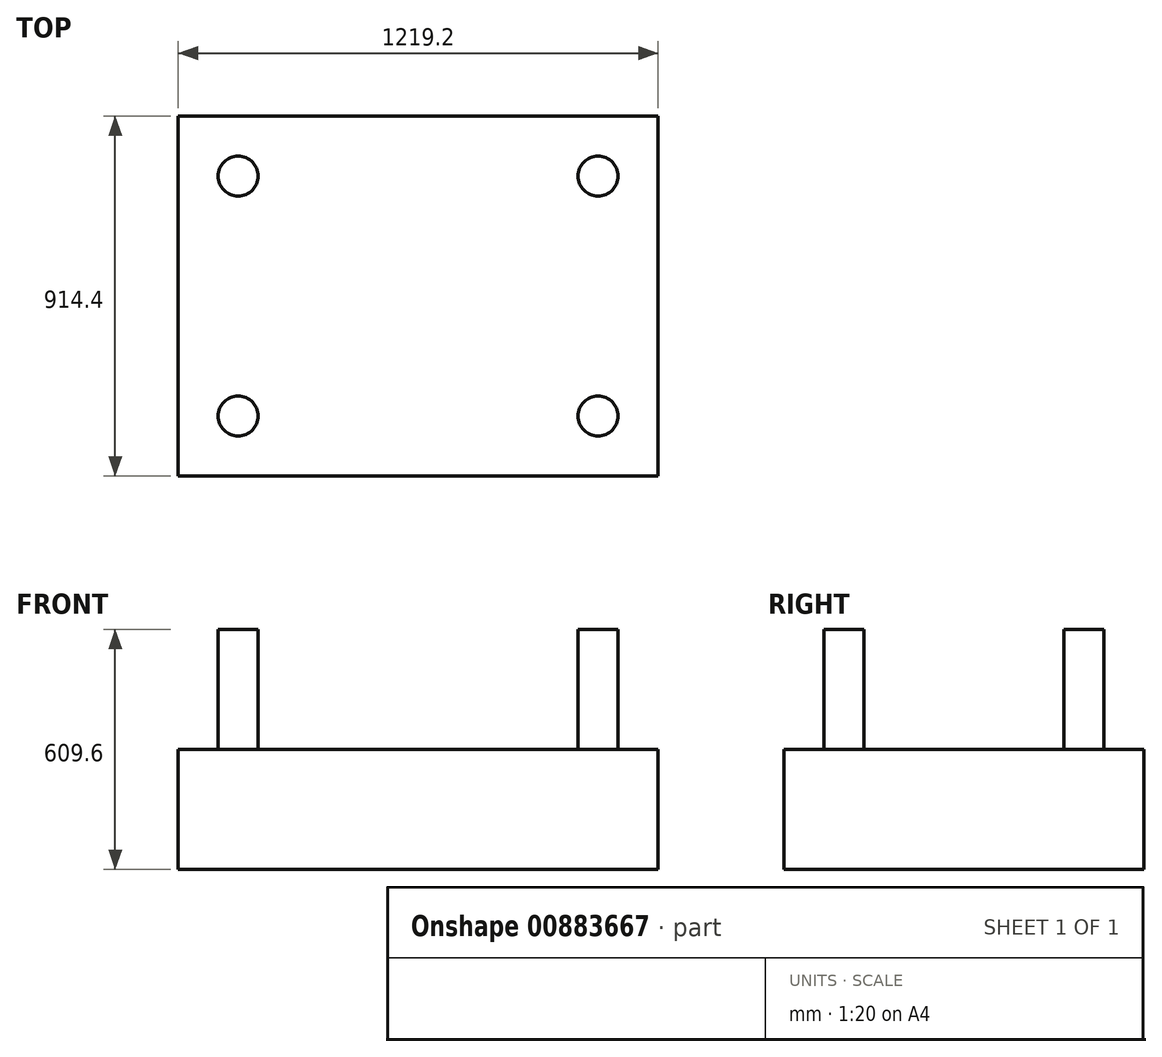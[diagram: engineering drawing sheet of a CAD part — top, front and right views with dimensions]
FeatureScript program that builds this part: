
annotation { "Feature Type Name" : "Feature", "Feature Type Description" : "" }
export const myFeature = defineFeature(function(context is Context, id is Id, definition is map)
    precondition{}
    {
        {
            var Q0;
            Q0=qCreatedBy(makeId("Top.planeOp"),FACE);
            var sketch = newSketch(context, id + "F0", { "sketchPlane" : qUnion([Q0])});
            skLineSegment(sketch, "E0.bottom", {"start": v(609.6, 457.2) * mm, "end": v(-609.6, 457.2) * mm});
            skLineSegment(sketch, "E0.top", {"start": v(609.6, -457.2) * mm, "end": v(-609.6, -457.2) * mm});
            skLineSegment(sketch, "E0.left", {"start": v(609.6, 457.2) * mm, "end": v(609.6, -457.2) * mm});
            skLineSegment(sketch, "E0.right", {"start": v(-609.6, 457.2) * mm, "end": v(-609.6, -457.2) * mm});
            skPoint(sketch, "E0.middle", {"position": v(0, 0) * mm});
            skSolve(sketch);
        }
        {
            var Q0;
            Q0=makeQuery(id+"F0.imprint","IMPRINT",FACE,{"disambiguationData":[TD([[makeQuery(id+"F0.imprint","IMPRINT",EDGE,{"derivedFrom":sQuery(id+"F0.wireOp",EDGE,"E0.bottom")}),1.0]])]});
            extrude(context, id + "F1", {"entities" : qUnion([Q0]), "depth" : 304.8 * mm, "offsetDistance" : 25.4 * mm});
        }
        {
            var Q0;
            Q0=makeQuery(id+"F1.opExtrude","CAP_FACE",FACE,{"disambiguationData":[OSD([sQuery(id+"F0.wireOp",EDGE,"E0.bottom"),sQuery(id+"F0.wireOp",EDGE,"E0.top"),sQuery(id+"F0.wireOp",EDGE,"E0.left"),sQuery(id+"F0.wireOp",EDGE,"E0.right")])],"isStart":false});
            var sketch = newSketch(context, id + "F2", { "sketchPlane" : qUnion([Q0])});
            skPoint(sketch, "E1", {"position": v(-457.2, 304.8) * mm});
            skPoint(sketch, "E2", {"position": v(457.2, 304.8) * mm});
            skPoint(sketch, "E3", {"position": v(-457.2, -304.8) * mm});
            skPoint(sketch, "E4", {"position": v(457.2, -304.8) * mm});
            skCircle(sketch, "E5", {"center": v(-457.2, 304.8) * mm, "radius": 50.8 * mm});
            skCircle(sketch, "E6", {"center": v(457.2, 304.8) * mm, "radius": 50.8 * mm});
            skCircle(sketch, "E7", {"center": v(-457.2, -304.8) * mm, "radius": 50.8 * mm});
            skCircle(sketch, "E8", {"center": v(457.2, -304.8) * mm, "radius": 50.8 * mm});
            skSolve(sketch);
        }
        {
            var Q0;
            Q0=makeQuery(id+"F2.imprint","IMPRINT",FACE,{"disambiguationData":[TD([[makeQuery(id+"F2.imprint","IMPRINT",EDGE,{"derivedFrom":sQuery(id+"F2.wireOp",EDGE,"E5")}),1.0]])]});
            var Q1;
            Q1=makeQuery(id+"F2.imprint","IMPRINT",FACE,{"disambiguationData":[TD([[makeQuery(id+"F2.imprint","IMPRINT",EDGE,{"derivedFrom":sQuery(id+"F2.wireOp",EDGE,"E6")}),1.0]])]});
            var Q2;
            Q2=makeQuery(id+"F2.imprint","IMPRINT",FACE,{"disambiguationData":[TD([[makeQuery(id+"F2.imprint","IMPRINT",EDGE,{"derivedFrom":sQuery(id+"F2.wireOp",EDGE,"E8")}),1.0]])]});
            var Q3;
            Q3=makeQuery(id+"F2.imprint","IMPRINT",FACE,{"disambiguationData":[TD([[makeQuery(id+"F2.imprint","IMPRINT",EDGE,{"derivedFrom":sQuery(id+"F2.wireOp",EDGE,"E7")}),1.0]])]});
            extrude(context, id + "F3", {"entities" : qUnion([Q0, Q1, Q2, Q3]), "operationType" : NewBodyOperationType.ADD, "depth" : 304.8 * mm, "offsetDistance" : 25.4 * mm});
        }
    });
